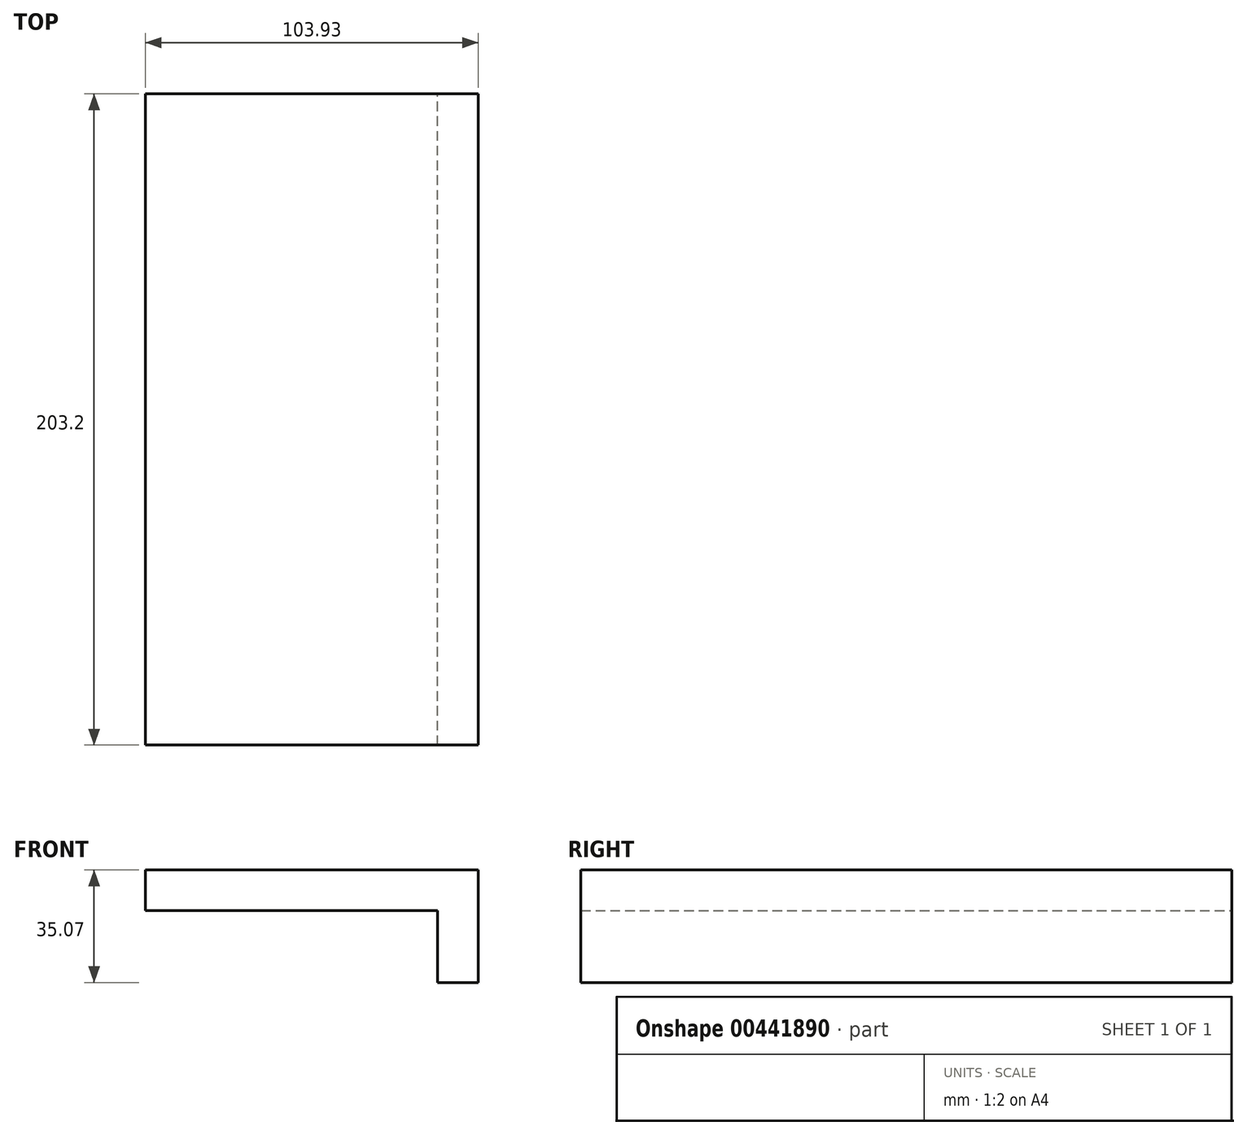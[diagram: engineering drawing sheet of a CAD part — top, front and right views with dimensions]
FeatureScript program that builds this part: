
annotation { "Feature Type Name" : "Feature", "Feature Type Description" : "" }
export const myFeature = defineFeature(function(context is Context, id is Id, definition is map)
    precondition{}
    {
        {
            var Q0;
            Q0=qCreatedBy(makeId("Front.planeOp"),FACE);
            var sketch = newSketch(context, id + "F0", { "sketchPlane" : qUnion([Q0])});
            skLineSegment(sketch, "E0", {"start": v(0, 0) * mm, "end": v(91.23, 0) * mm});
            skLineSegment(sketch, "E1", {"start": v(91.23, 0) * mm, "end": v(91.23, -22.37) * mm});
            skLineSegment(sketch, "E2.0", {"start": v(103.93, 12.7) * mm, "end": v(103.93, -22.37) * mm});
            skLineSegment(sketch, "E2.1", {"start": v(0, 12.7) * mm, "end": v(103.93, 12.7) * mm});
            skLineSegment(sketch, "E3", {"start": v(91.23, -22.37) * mm, "end": v(103.93, -22.37) * mm});
            skLineSegment(sketch, "E4", {"start": v(0, 12.7) * mm, "end": v(0, 0) * mm});
            skSolve(sketch);
        }
        {
            var Q0;
            Q0=makeQuery(id+"F0.imprint","IMPRINT",FACE,{"disambiguationData":[TD([[makeQuery(id+"F0.imprint","IMPRINT",EDGE,{"derivedFrom":sQuery(id+"F0.wireOp",EDGE,"E0")}),1.0]])]});
            extrude(context, id + "F1", {"entities" : qUnion([Q0]), "depth" : 203.2 * mm});
        }
    });
